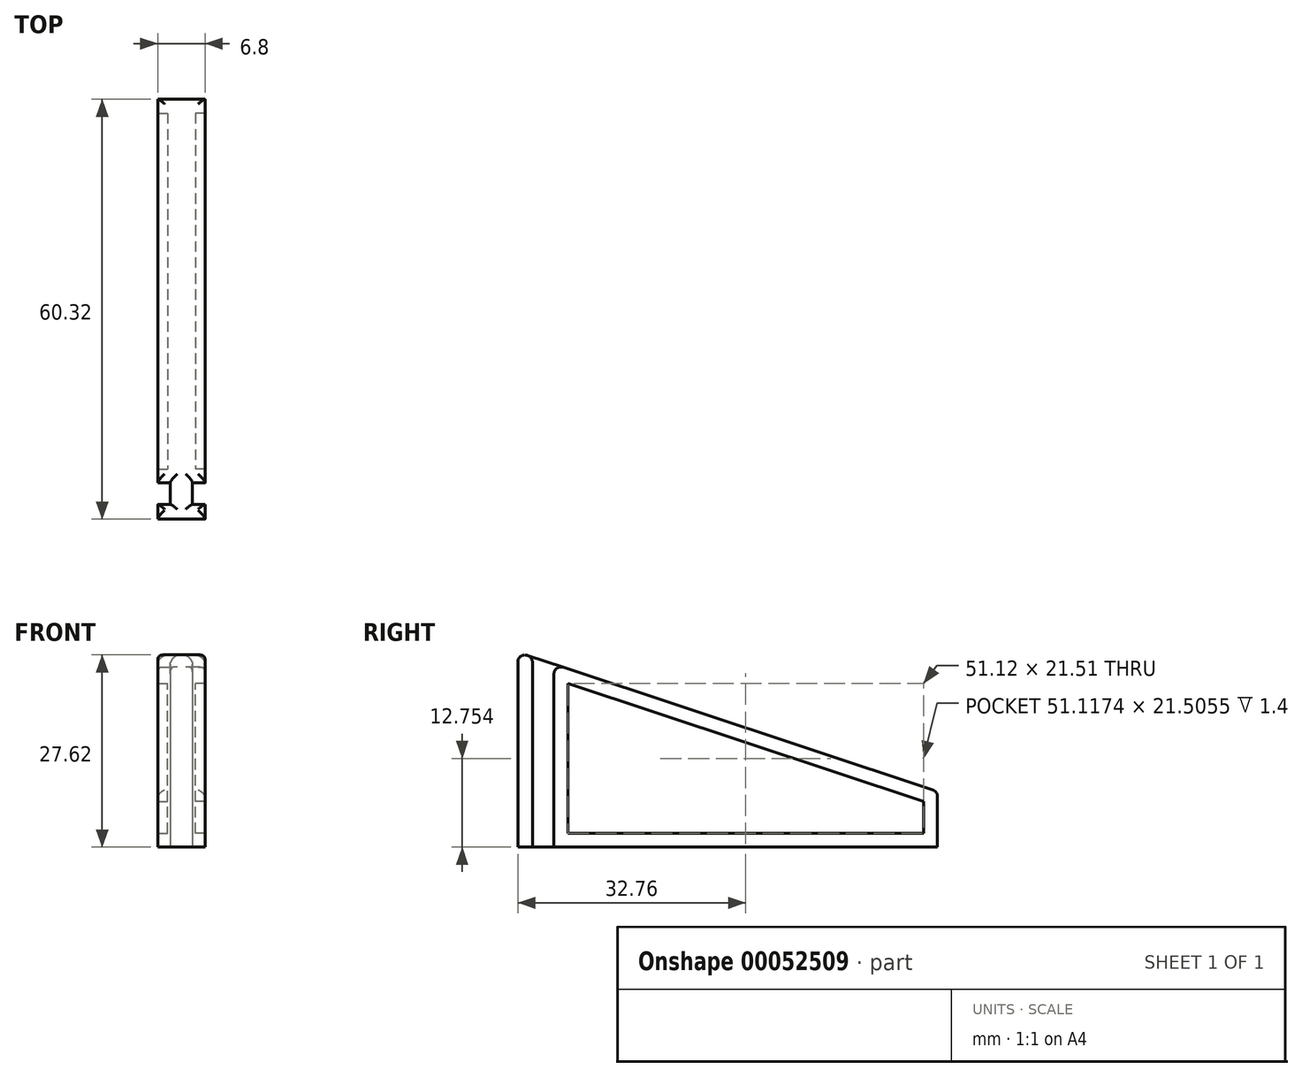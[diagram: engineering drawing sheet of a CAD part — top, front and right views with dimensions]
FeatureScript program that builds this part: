
annotation { "Feature Type Name" : "Feature", "Feature Type Description" : "" }
export const myFeature = defineFeature(function(context is Context, id is Id, definition is map)
    precondition{}
    {
        {
            var Q0;
            Q0=qCreatedBy(makeId("Right.planeOp"),FACE);
            var sketch = newSketch(context, id + "F0", { "sketchPlane" : qUnion([Q0])});
            skLineSegment(sketch, "E0", {"start": v(-55.48, 59.86) * mm, "end": v(-55.48, 31.86) * mm});
            skLineSegment(sketch, "E1", {"start": v(-55.48, 31.86) * mm, "end": v(4.84, 31.86) * mm});
            skLineSegment(sketch, "E2", {"start": v(4.84, 31.86) * mm, "end": v(4.84, 39.86) * mm});
            skLineSegment(sketch, "E3", {"start": v(4.84, 39.86) * mm, "end": v(-55.48, 59.86) * mm});
            skLineSegment(sketch, "E4", {"start": v(-53.38, 59.16) * mm, "end": v(-53.38, 31.86) * mm});
            skLineSegment(sketch, "E5", {"start": v(-50.28, 58.14) * mm, "end": v(-50.28, 31.86) * mm});
            skSolve(sketch);
        }
        {
            var Q0;
            {var subQ0=sQuery(id+"F0.wireOp",EDGE,"E4");Q0=makeQuery(id+"F0.imprint","IMPRINT",FACE,{"disambiguationData":[TD([[makeQuery(id+"F0.imprint","IMPRINT",EDGE,{"derivedFrom":subQ0}),1.0]])]});}
            extrude(context, id + "F1", {"entities" : qUnion([Q0]), "offsetDistance" : 25 * mm, "depth" : 1.6 * mm});
        }
        {
            var Q0;
            {var subQ0=sQuery(id+"F0.wireOp",EDGE,"E2");Q0=makeQuery(id+"F0.imprint","IMPRINT",FACE,{"disambiguationData":[TD([[makeQuery(id+"F0.imprint","IMPRINT",EDGE,{"derivedFrom":subQ0}),1.0]])]});}
            var Q1;
            {var subQ0=sQuery(id+"F0.wireOp",EDGE,"E0");Q1=makeQuery(id+"F0.imprint","IMPRINT",FACE,{"disambiguationData":[TD([[makeQuery(id+"F0.imprint","IMPRINT",EDGE,{"derivedFrom":subQ0}),1.0]])]});}
            extrude(context, id + "F2", {"entities" : qUnion([Q0, Q1]), "operationType" : NewBodyOperationType.ADD, "offsetDistance" : 25 * mm, "depth" : 3.4 * mm});
        }
        {
            var Q0;
            Q0=makeQuery(id+"F2.opExtrude","CAP_FACE",FACE,{"disambiguationData":[OSD([sQuery(id+"F0.wireOp",EDGE,"E1"),sQuery(id+"F0.wireOp",EDGE,"E2"),sQuery(id+"F0.wireOp",EDGE,"E3"),sQuery(id+"F0.wireOp",EDGE,"E5")])],"isStart":false});
            shell(context, id + "F3", {"entities" : qUnion([Q0]), "thickness" : 2 * mm});
        }
        {
            var Q0;
            Q0=makeQuery(id+"F1.opExtrude","SWEPT_BODY",BODY,{"disambiguationData":[OSD([sQuery(id+"F0.wireOp",EDGE,"E1"),sQuery(id+"F0.wireOp",EDGE,"E3"),sQuery(id+"F0.wireOp",EDGE,"E4"),sQuery(id+"F0.wireOp",EDGE,"E5")])]});
            var Q1;
            {var subQ0=sQuery(id+"F0.wireOp",EDGE,"E2");Q1=makeQuery(id+"F0.imprint","IMPRINT",FACE,{"disambiguationData":[TD([[makeQuery(id+"F0.imprint","IMPRINT",EDGE,{"derivedFrom":subQ0}),1.0]])]});}
            mirror(context, id + "F4", {"operationType" : NewBodyOperationType.ADD, "entities" : qUnion([Q0]), "mirrorPlane" : qUnion([Q1])});
        }
        {
            var Q0;
            {var subQ0=sQuery(id+"F0.wireOp",EDGE,"E3");var subQ1=makeQuery(id+"F2.boolean.opBoolean","MERGE",FACE,{"derivedFrom":[makeQuery(id+"F1.opExtrude","SWEPT_FACE",FACE,{"disambiguationData":[OSD([subQ0])]}),makeQuery(id+"F2.opExtrude","SWEPT_FACE",FACE,{"disambiguationData":[OSD([subQ0]),TDD([makeQuery(id+"F0.imprint","IMPRINT",EDGE,{"disambiguationData":[TD([[makeQuery(id+"F0.imprint","INTERSECT",VERTEX,{"derivedFrom":[sQuery(id+"F0.wireOp",EDGE,"E2"),subQ0]}),-1.0]])],"derivedFrom":subQ0})])]}),makeQuery(id+"F2.opExtrude","SWEPT_FACE",FACE,{"disambiguationData":[OSD([subQ0]),TDD([makeQuery(id+"F0.imprint","IMPRINT",EDGE,{"disambiguationData":[TD([[makeQuery(id+"F0.imprint","INTERSECT",VERTEX,{"derivedFrom":[sQuery(id+"F0.wireOp",EDGE,"E0"),subQ0]}),1.0]])],"derivedFrom":subQ0})])]})]});Q0=makeQuery(id+"F4.boolean.opBoolean","MERGE",FACE,{"derivedFrom":[subQ1,makeQuery(id+"F4.opPattern","COPY",FACE,{"derivedFrom":subQ1,"instanceName":"1"})]});}
            fillet(context, id + "F5", {"entities" : qUnion([Q0]), "radius" : 1 * mm, "tangentPropagation" : true, "defaultsChanged" : false, "vertexSettings" : [], "allowEdgeOverflow" : false});
        }
    });
